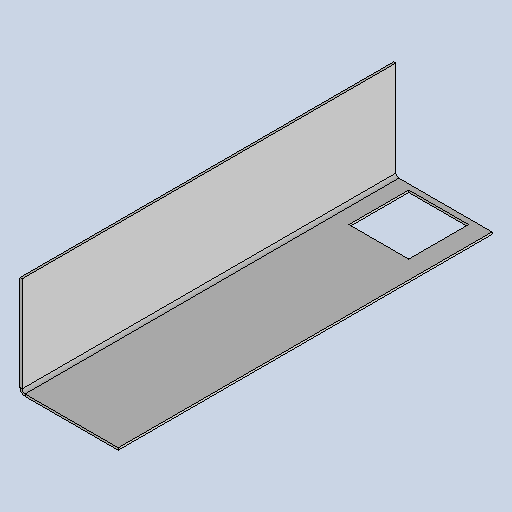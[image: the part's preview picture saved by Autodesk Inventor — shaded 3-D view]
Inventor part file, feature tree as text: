
AUTODESK INVENTOR PART (.ipt)
format: ipt  version: 2025.1 (Build 291241020, 241B)  size: 166,912 bytes
history: native  units: mm
features: sheet_metal_op x4, other x4, sketch x3
ambient origin geometry x8: Origin, YZ Plane, XZ Plane, XY Plane, X Axis, Y Axis, Z Axis, Center Point
bodies: Body1 (feature_tree)
feature tree (11):
  sheet_metal_op  "Face3"
  sheet_metal_op  "Flange3"
  sketch  "Sketch1"  dims[d154=92.0mm]
  other  "Plate5"
  sketch  "Sketch7"  dims[d155=350.0mm]
  other  "Plate6"
  sheet_metal_op  "Bend3"
  sheet_metal_op  "Corner3"
  sketch  "Sketch8"  dims[d156=2.0mm d157=2.0mm d158=1.0mm d159=4.0mm d160=2.75mm d161=94.0mm d162=90.0deg d163=2.75mm d164=8.0mm d165=2.0mm d166=2.75mm d167=56.0mm d168=56.0mm d169=5.0mm d170=2.0mm d171=0.0mm d172=17.0mm]
  other  "Cut1"
  other  "Definition1"
